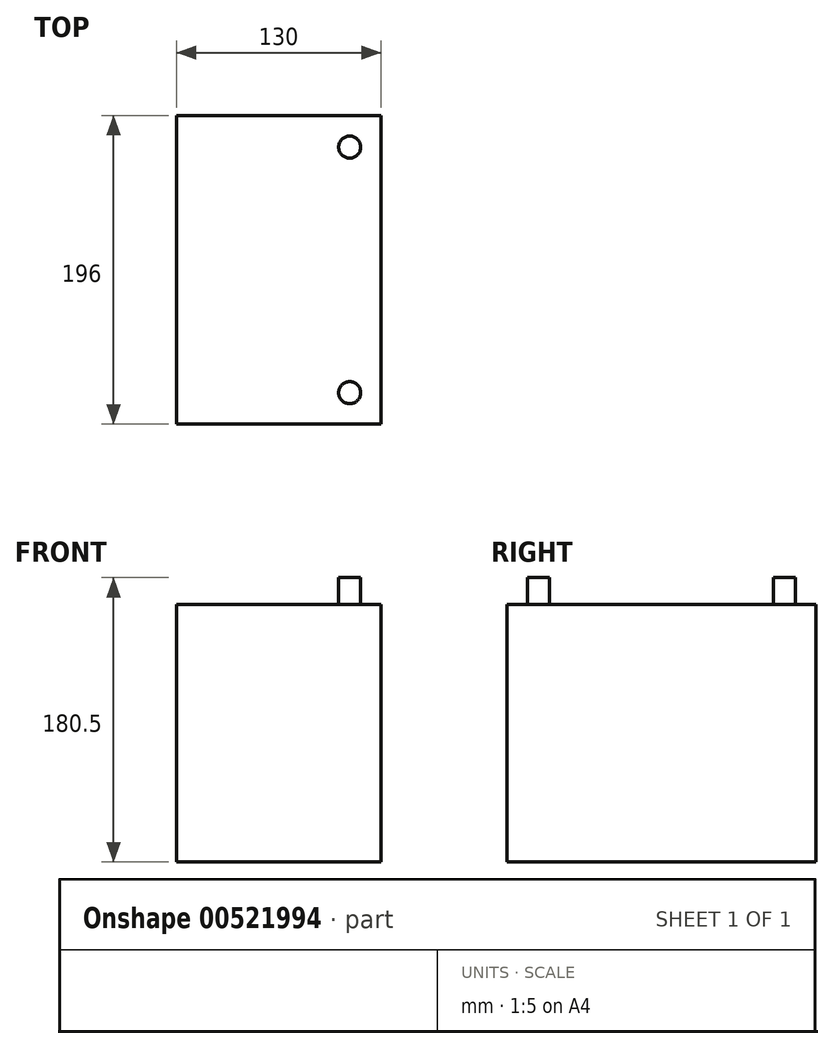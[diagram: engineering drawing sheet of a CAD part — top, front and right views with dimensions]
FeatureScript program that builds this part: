
annotation { "Feature Type Name" : "Feature", "Feature Type Description" : "" }
export const myFeature = defineFeature(function(context is Context, id is Id, definition is map)
    precondition{}
    {
        {
            var Q0;
            Q0=qCreatedBy(makeId("Top.planeOp"),FACE);
            var sketch = newSketch(context, id + "F0", { "sketchPlane" : qUnion([Q0])});
            skLineSegment(sketch, "E0.bottom", {"start": v(0, 0) * mm, "end": v(130, 0) * mm});
            skLineSegment(sketch, "E0.top", {"start": v(0, -196) * mm, "end": v(130, -196) * mm});
            skLineSegment(sketch, "E0.left", {"start": v(0, 0) * mm, "end": v(0, -196) * mm});
            skLineSegment(sketch, "E0.right", {"start": v(130, 0) * mm, "end": v(130, -196) * mm});
            skSolve(sketch);
        }
        {
            var Q0;
            Q0=makeQuery(id+"F0.imprint","IMPRINT",FACE,{"disambiguationData":[TD([[makeQuery(id+"F0.imprint","IMPRINT",EDGE,{"derivedFrom":sQuery(id+"F0.wireOp",EDGE,"E0.bottom")}),-1.0]])]});
            extrude(context, id + "F1", {"entities" : qUnion([Q0]), "depth" : 163.5 * mm, "offsetDistance" : 25 * mm});
        }
        {
            var Q0;
            Q0=makeQuery(id+"F1.opExtrude","CAP_FACE",FACE,{"disambiguationData":[OSD([sQuery(id+"F0.wireOp",EDGE,"E0.bottom"),sQuery(id+"F0.wireOp",EDGE,"E0.top"),sQuery(id+"F0.wireOp",EDGE,"E0.left"),sQuery(id+"F0.wireOp",EDGE,"E0.right")])],"isStart":false});
            var sketch = newSketch(context, id + "F2", { "sketchPlane" : qUnion([Q0])});
            skCircle(sketch, "E1", {"center": v(110, -176) * mm, "radius": 7 * mm});
            skCircle(sketch, "E2", {"center": v(110, -20) * mm, "radius": 7 * mm});
            skLineSegment(sketch, "E3", {"start": v(110, -20) * mm, "end": v(110, -176) * mm, "construction": true});
            skSolve(sketch);
        }
        {
            var Q0;
            Q0=makeQuery(id+"F2.imprint","IMPRINT",FACE,{"disambiguationData":[TD([[makeQuery(id+"F2.imprint","IMPRINT",EDGE,{"derivedFrom":sQuery(id+"F2.wireOp",EDGE,"E1")}),1.0]])]});
            var Q1;
            Q1=makeQuery(id+"F2.imprint","IMPRINT",FACE,{"disambiguationData":[TD([[makeQuery(id+"F2.imprint","IMPRINT",EDGE,{"derivedFrom":sQuery(id+"F2.wireOp",EDGE,"E2")}),1.0]])]});
            extrude(context, id + "F3", {"entities" : qUnion([Q0, Q1]), "operationType" : NewBodyOperationType.ADD, "depth" : (180.5 - 163.5) * mm, "offsetDistance" : 25 * mm});
        }
    });
